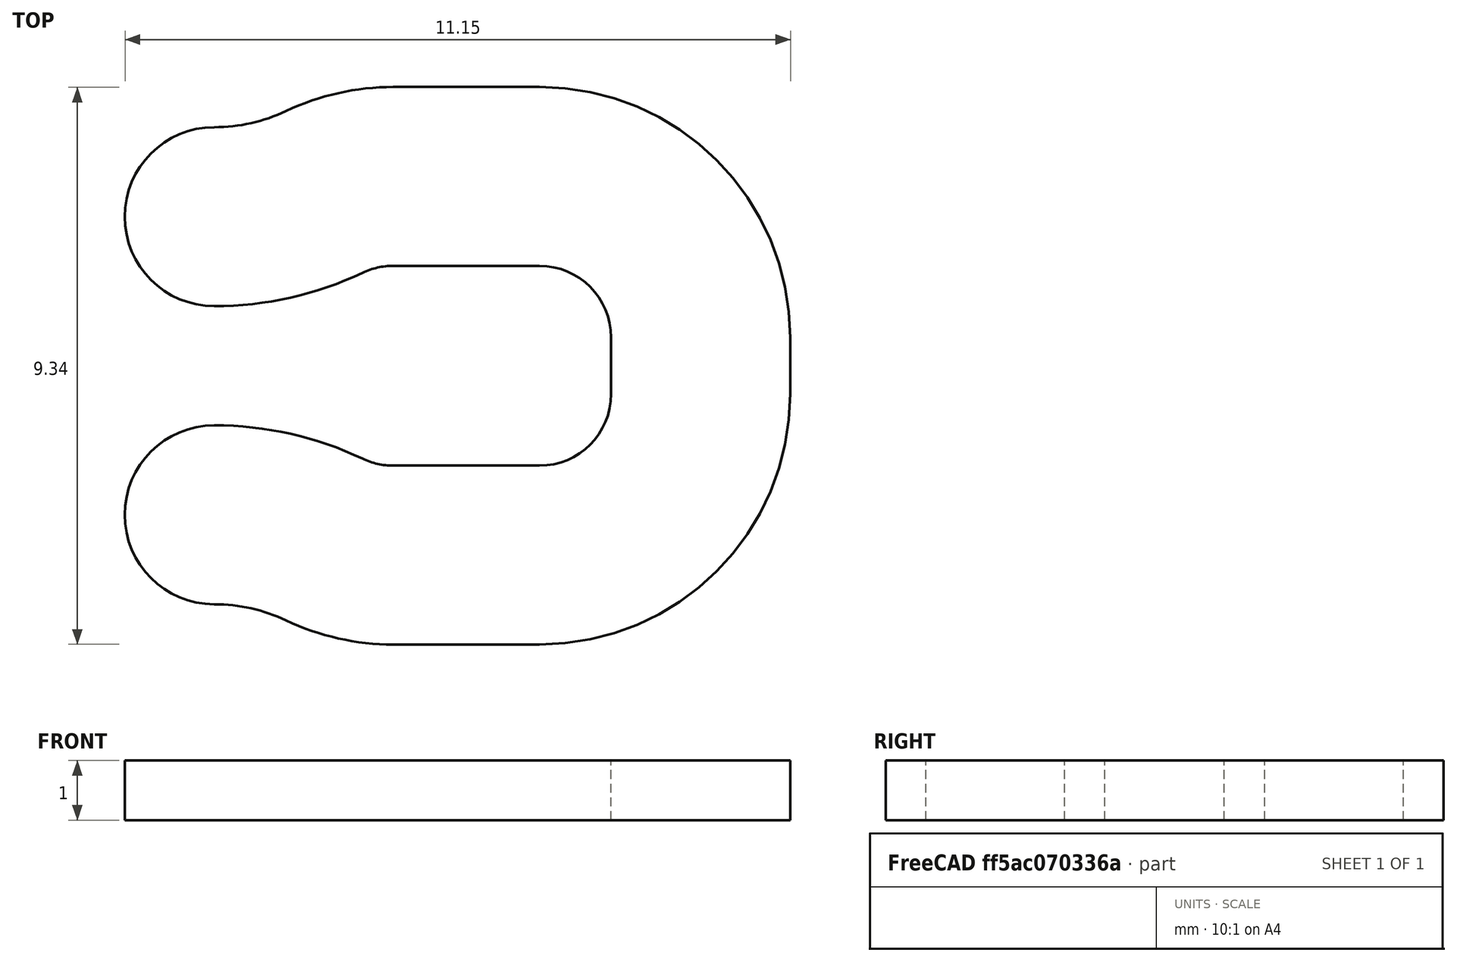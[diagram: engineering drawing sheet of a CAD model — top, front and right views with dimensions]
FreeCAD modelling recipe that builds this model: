
FCSTD DOCUMENT  (FreeCAD 1.0R39319 (Git))
Label: temp-sensor-thermal-relief
License: All rights reserved
LicenseURL: https://en.wikipedia.org/wiki/All_rights_reserved
objects: Sketcher::SketchObject×1, PartDesign::Pad×1, PartDesign::Body×1
note: 6 computed .brp shape members not serialized (recipe doc carries the construction recipe); baked Part::Feature solids carry a one-line shape summary decoded from their .brp

FEATURE [Sketcher::SketchObject] Sketch
  ArcFitTolerance = 1e-06
  AttachmentSupport = -> [XY_Plane]
  FullyConstrained = true
  MakeInternals = false
  MapMode = 5
  sketch-geometry (28):
    g0: ArcOfCircle CenterX=-1.225 CenterY=0.475 CenterZ=0 NormalX=0 NormalY=0 NormalZ=1 AngleXU=0 Radius=1.2 StartAngle=1.5708 EndAngle=2.01343
    g1: ArcOfCircle CenterX=-4.225 CenterY=6.80417 CenterZ=0 NormalX=0 NormalY=0 NormalZ=1 AngleXU=0 Radius=5.80417 StartAngle=4.71239 EndAngle=5.15502
    g2: ArcOfCircle CenterX=-4.225 CenterY=2.5 CenterZ=0 NormalX=0 NormalY=0 NormalZ=1 AngleXU=0 Radius=1.5 StartAngle=1.5708 EndAngle=4.71239
    g3: ArcOfCircle CenterX=-1.225 CenterY=0.475 CenterZ=0 NormalX=0 NormalY=0 NormalZ=1 AngleXU=0 Radius=4.2 StartAngle=1.5708 EndAngle=2.01343
    g4: LineSegment [constr] StartX=-1.225 StartY=0.475 StartZ=0 EndX=-1.225 EndY=4.675 EndZ=0
    g5: LineSegment [constr] StartX=-3.02393 StartY=4.27024 StartZ=0 EndX=-1.225 EndY=0.475 EndZ=0
    g6: ArcOfCircle CenterX=-4.225 CenterY=6.80417 CenterZ=0 NormalX=0 NormalY=0 NormalZ=1 AngleXU=0 Radius=2.80417 StartAngle=4.71239 EndAngle=5.15502
    g7: LineSegment StartX=-1.225 StartY=4.675 StartZ=0 EndX=1.22501 EndY=4.675 EndZ=0
    g8: LineSegment StartX=-1.225 StartY=1.675 StartZ=0 EndX=1.22501 EndY=1.675 EndZ=0
    g9: ArcOfCircle CenterX=1.225 CenterY=0.475 CenterZ=0 NormalX=0 NormalY=0 NormalZ=1 AngleXU=0 Radius=1.2 StartAngle=0 EndAngle=1.57079
    g10: ArcOfCircle CenterX=1.225 CenterY=0.475 CenterZ=0 NormalX=0 NormalY=0 NormalZ=1 AngleXU=0 Radius=4.2 StartAngle=0 EndAngle=1.57079
    g11: LineSegment [constr] StartX=-1.225 StartY=-0.475 StartZ=0 EndX=-1.225 EndY=0.475 EndZ=0
    g12: LineSegment [constr] StartX=-1.225 StartY=0.475 StartZ=0 EndX=1.225 EndY=0.475 EndZ=0
    g13: LineSegment [constr] StartX=1.225 StartY=0.475 StartZ=0 EndX=1.225 EndY=-0.475 EndZ=0
    g14: LineSegment [constr] StartX=1.225 StartY=-0.475 StartZ=0 EndX=-1.225 EndY=-0.475 EndZ=0
    g15: ArcOfCircle CenterX=-1.225 CenterY=-0.475 CenterZ=0 NormalX=0 NormalY=0 NormalZ=1 AngleXU=0 Radius=1.2 StartAngle=4.26976 EndAngle=4.71239
    g16: ArcOfCircle CenterX=-4.225 CenterY=-6.80417 CenterZ=0 NormalX=0 NormalY=0 NormalZ=1 AngleXU=0 Radius=5.80417 StartAngle=1.12817 EndAngle=1.5708
    g17: ArcOfCircle CenterX=-4.225 CenterY=-2.5 CenterZ=0 NormalX=0 NormalY=0 NormalZ=1 AngleXU=0 Radius=1.5 StartAngle=1.5708 EndAngle=4.71239
    g18: ArcOfCircle CenterX=-1.225 CenterY=-0.475 CenterZ=0 NormalX=0 NormalY=0 NormalZ=1 AngleXU=0 Radius=4.2 StartAngle=4.26976 EndAngle=4.71239
    g19: LineSegment [constr] StartX=-1.225 StartY=-0.475 StartZ=0 EndX=-1.225 EndY=-4.675 EndZ=0
    g20: LineSegment [constr] StartX=-3.02393 StartY=-4.27024 StartZ=0 EndX=-1.225 EndY=-0.475 EndZ=0
    g21: ArcOfCircle CenterX=-4.225 CenterY=-6.80417 CenterZ=0 NormalX=0 NormalY=0 NormalZ=1 AngleXU=0 Radius=2.80417 StartAngle=1.12817 EndAngle=1.5708
    g22: LineSegment StartX=-1.225 StartY=-4.675 StartZ=0 EndX=1.225 EndY=-4.675 EndZ=0
    g23: LineSegment StartX=-1.225 StartY=-1.675 StartZ=0 EndX=1.225 EndY=-1.675 EndZ=0
    g24: ArcOfCircle CenterX=1.225 CenterY=-0.475 CenterZ=0 NormalX=0 NormalY=0 NormalZ=1 AngleXU=0 Radius=1.2 StartAngle=4.71239 EndAngle=6.28319
    g25: ArcOfCircle CenterX=1.225 CenterY=-0.475 CenterZ=0 NormalX=0 NormalY=0 NormalZ=1 AngleXU=0 Radius=4.2 StartAngle=4.71239 EndAngle=6.28319
    g26: LineSegment StartX=2.425 StartY=0.475 StartZ=0 EndX=2.425 EndY=-0.475 EndZ=0
    g27: LineSegment StartX=5.425 StartY=-0.475 StartZ=0 EndX=5.425 EndY=0.475 EndZ=0
  constraints (65):
    c: Symmetric(g0,g9,g-2)
    c: Tangent(g1,g0) = 1.5708
    c: Vertical(g2,g2)
    c: Coincident(g4,g3)
    c: Vertical(g4)
    c: PointOnObject(g0,g4)
    c: Coincident(g5,g3)
    c: Coincident(g6,g1)
    c: Equal(g8,g7)
    c: Coincident(g10,g9)
    c: Coincident(g10,g7)
    c: Coincident(g9,g8)
    c: Radius(g2) = 1.5
    c: Radius(g0) = 1.2
    c: DistanceY(g-1,g1) = 1
    c: Tangent(g2,g6) = 1.5708
    c: Tangent(g7,g3) = 1.5708
    c: Tangent(g8,g0) = 1.5708
    c: Tangent(g6,g3) = 1.5708
    c: Tangent(g2,g1) = -1.5708
    c: DistanceX(g1,g0) = 3
    c: Coincident(g11,g12)
    c: Coincident(g12,g13)
    c: Coincident(g13,g14)
    c: Coincident(g14,g11)
    c: Vertical(g11)
    c: Horizontal(g12)
    c: Coincident(g15,g11)
    c: Tangent(g16,g15) = 1.5708
    c: Coincident(g18,g11)
    c: Coincident(g19,g11)
    c: Coincident(g19,g18)
    c: Vertical(g19)
    c: PointOnObject(g15,g19)
    c: Coincident(g20,g18)
    c: Coincident(g20,g11)
    c: Coincident(g21,g16)
    c: Equal(g14,g23)
    c: Equal(g23,g22)
    c: Coincident(g25,g24)
    c: Coincident(g25,g22)
    c: Coincident(g24,g13)
    c: Coincident(g24,g23)
    c: Radius(g15) = 1.2
    c: Tangent(g17,g21) = 1.5708
    c: Tangent(g22,g18) = -1.5708
    c: Tangent(g23,g15) = -1.5708
    c: Tangent(g21,g18) = 1.5708
    c: Tangent(g17,g16) = -1.5708
    c: Tangent(g26,g9) = 1.5708
    c: Coincident(g26,g24)
    c: Coincident(g27,g25)
    c: Tangent(g27,g10) = -1.5708
    c: Symmetric(g11,g13,g-2)
    c: Symmetric(g13,g9,g-1)
    c: Coincident(g3,g4)
    c: Coincident(g3,g5)
    c: Coincident(g3,g11)
    c: Coincident(g12,g9)
    c: DistanceX(g12,g12) = 2.45
    c: DistanceY(g13,g13) = 0.95
    c: Symmetric(g16,g1,g-1)
    c: Vertical(g17,g17)
    c: Symmetric(g24,g9,g-1)
    c: Symmetric(g25,g10,g-1)
FEATURE [PartDesign::Pad] Pad
  Direction = (0,0,1)
  Length = 1
  Length2 = 10
  Profile = -> Sketch
  ReferenceAxis = -> Sketch [N_Axis]
  Refine = true
  Suppressed = false
  Type = 0
FEATURE [PartDesign::Body] Body
  AllowCompound = false
  Group = -> [Sketch,Pad]
  Origin = -> Origin
  Tip = -> Pad
